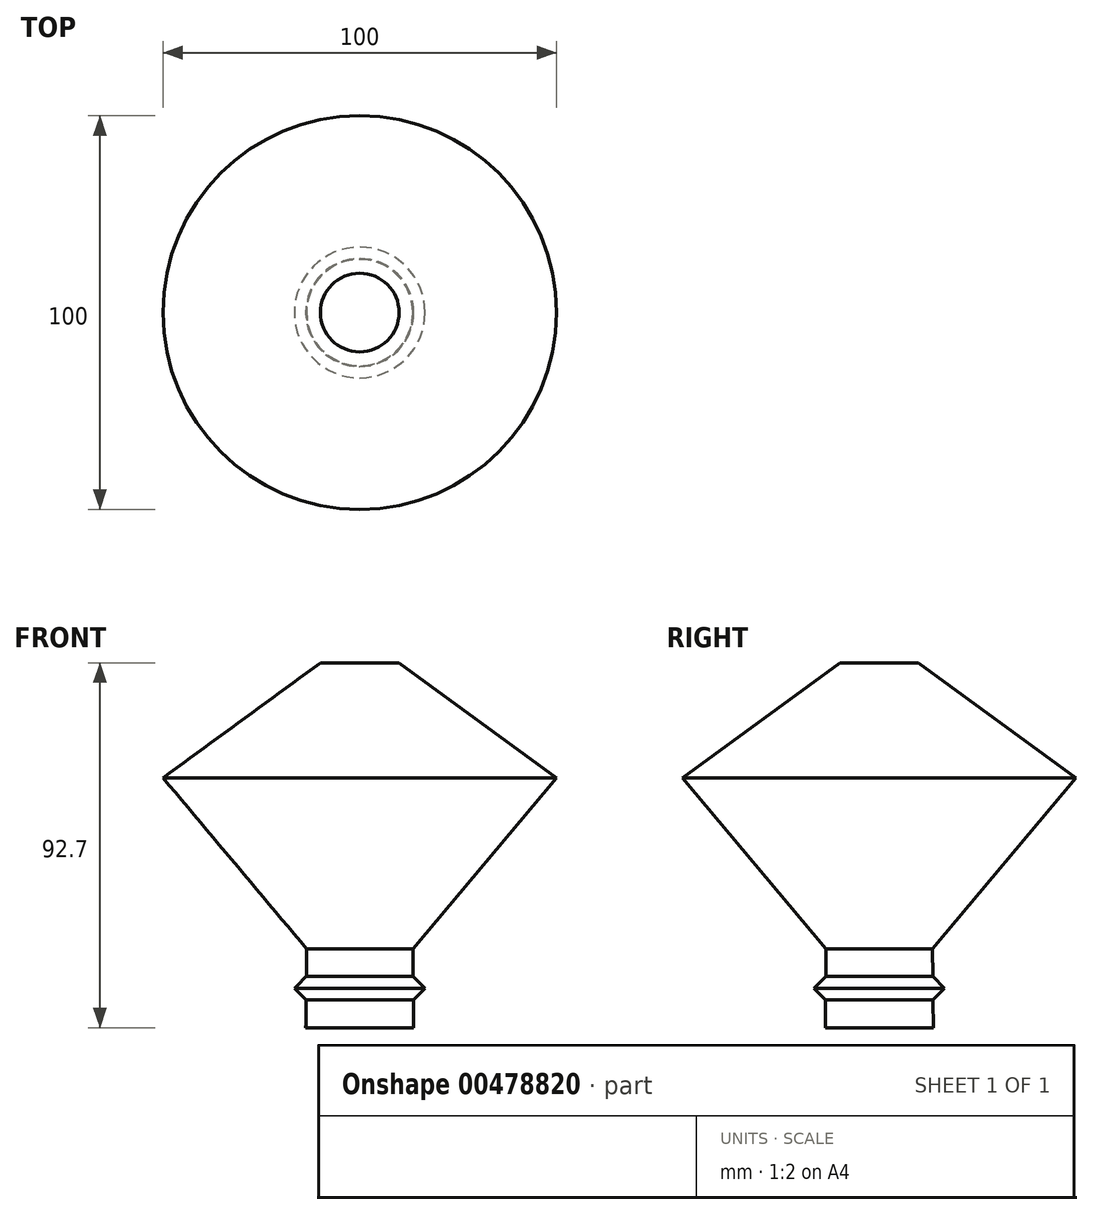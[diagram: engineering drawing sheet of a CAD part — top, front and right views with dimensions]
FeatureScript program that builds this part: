
annotation { "Feature Type Name" : "Feature", "Feature Type Description" : "" }
export const myFeature = defineFeature(function(context is Context, id is Id, definition is map)
    precondition{}
    {
        {
            var Q0;
            Q0=qCreatedBy(makeId("Front.planeOp"),FACE);
            var sketch = newSketch(context, id + "F0", { "sketchPlane" : qUnion([Q0])});
            skLineSegment(sketch, "E0", {"start": v(0, 0) * mm, "end": v(13.7, 0) * mm});
            skLineSegment(sketch, "E1", {"start": v(13.7, 0) * mm, "end": v(13.63, 7) * mm});
            skLineSegment(sketch, "E2", {"start": v(13.6, 10) * mm, "end": v(16.6, 10) * mm, "construction": true});
            skLineSegment(sketch, "E3", {"start": v(16.6, 10) * mm, "end": v(13.57, 13) * mm});
            skLineSegment(sketch, "E4", {"start": v(16.6, 10) * mm, "end": v(13.63, 7) * mm});
            skLineSegment(sketch, "E5.trimOffspring", {"start": v(13.57, 13) * mm, "end": v(13.5, 20) * mm});
            skLineSegment(sketch, "E6", {"start": v(0, 100.94) * mm, "end": v(0, -100.94) * mm, "construction": true});
            skLineSegment(sketch, "E7", {"start": v(-123.06, 0) * mm, "end": v(123.06, 0) * mm, "construction": true});
            skLineSegment(sketch, "E8", {"start": v(13.5, 20) * mm, "end": v(50, 63.5) * mm});
            skLineSegment(sketch, "E9", {"start": v(50, 63.5) * mm, "end": v(0, 100) * mm});
            skLineSegment(sketch, "E10", {"start": v(0, 92.7) * mm, "end": v(10, 92.7) * mm});
            skSolve(sketch);
        }
        {
            var Q0;
            Q0=qCreatedBy(makeId("Front.planeOp"),FACE);
            var sketch = newSketch(context, id + "F1", { "sketchPlane" : qUnion([Q0])});
            skLineSegment(sketch, "E11.0", {"start": v(0, 92.7) * mm, "end": v(10, 92.7) * mm});
            skLineSegment(sketch, "E12.0", {"start": v(50, 63.5) * mm, "end": v(10, 92.7) * mm});
            skLineSegment(sketch, "E13.0", {"start": v(13.5, 20) * mm, "end": v(50, 63.5) * mm});
            skLineSegment(sketch, "E14.0", {"start": v(13.57, 13) * mm, "end": v(13.5, 20) * mm});
            skLineSegment(sketch, "E15.0", {"start": v(16.6, 10) * mm, "end": v(13.57, 13) * mm});
            skLineSegment(sketch, "E16.0", {"start": v(16.6, 10) * mm, "end": v(13.63, 7) * mm});
            skLineSegment(sketch, "E17.0", {"start": v(13.7, 0) * mm, "end": v(13.63, 7) * mm});
            skPoint(sketch, "E18.end.orphan", {"position": v(0, 100) * mm});
            skSolve(sketch);
        }
        {
            var Q0;
            Q0 = qSketchRegion(id + "F1", true);
            var Q1;
            Q1 = qBodyType(qCreatedBy(id + "F1" ,EDGE), BodyType.WIRE);
            var Q2;
            Q2=sQuery(id+"F0.wireOp",EDGE,"E6");
            revolve(context, id + "F2", {"bodyType" : ToolBodyType.SURFACE, "entities" : qUnion([Q0]), "surfaceEntities" : qUnion([Q1]), "axis" : qUnion([Q2]), "revolveType" : RevolveType.FULL});
        }
    });
